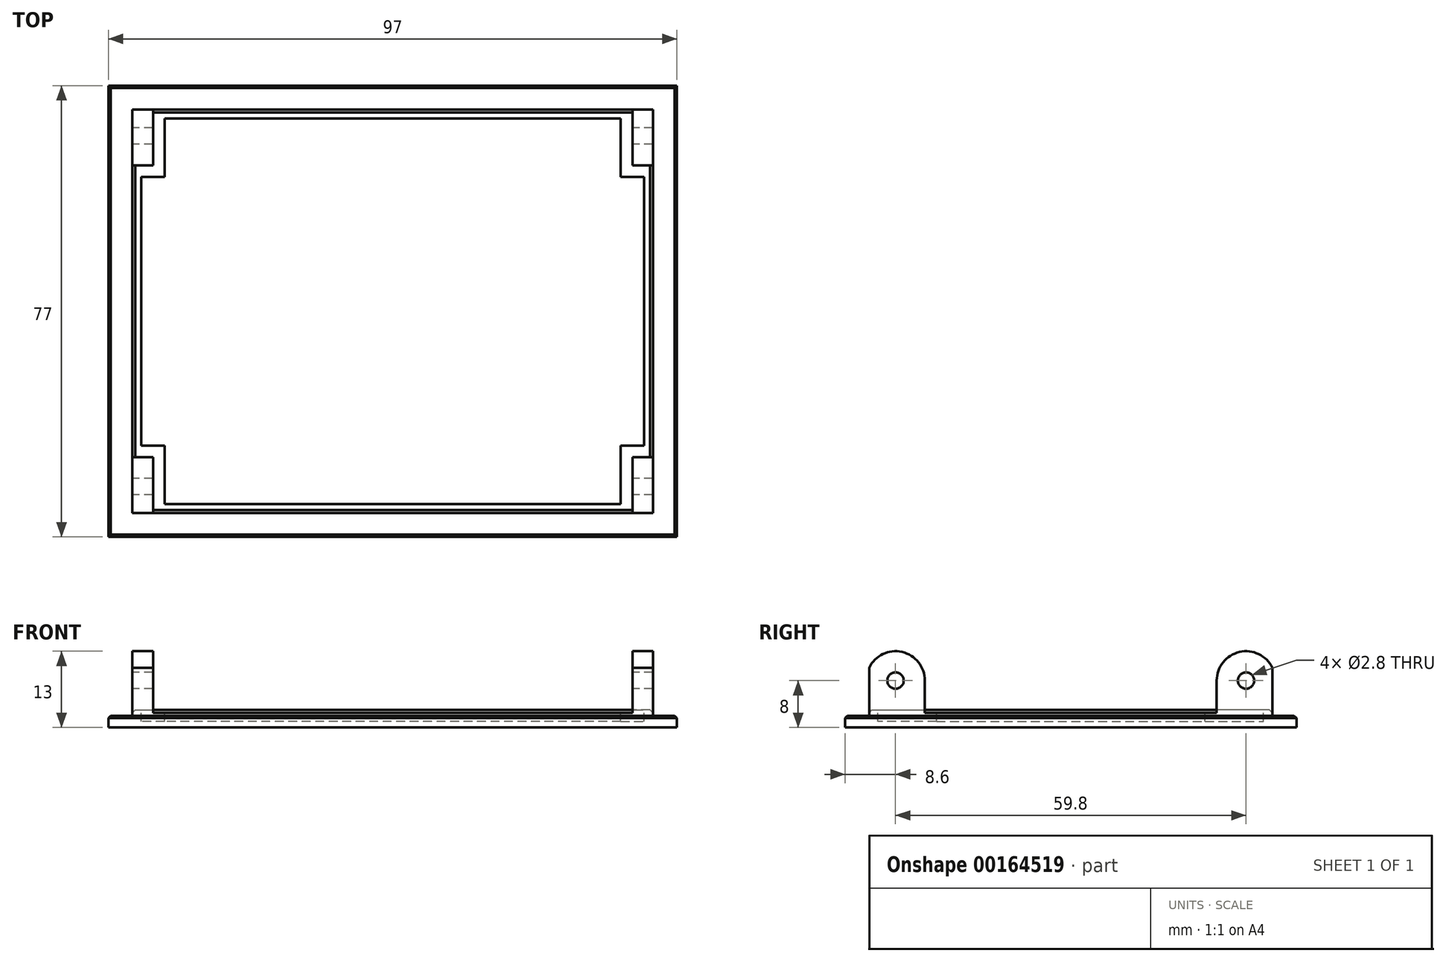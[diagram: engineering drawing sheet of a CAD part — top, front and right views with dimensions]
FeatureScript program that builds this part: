
annotation { "Feature Type Name" : "Feature", "Feature Type Description" : "" }
export const myFeature = defineFeature(function(context is Context, id is Id, definition is map)
    precondition{}
    {
        {
            var Q0;
            Q0=qCreatedBy(makeId("Top.planeOp"),FACE);
            var sketch = newSketch(context, id + "F0", { "sketchPlane" : qUnion([Q0])});
            skLineSegment(sketch, "E0.bottom", {"start": v(48.5, 38.5) * mm, "end": v(-48.5, 38.5) * mm});
            skLineSegment(sketch, "E0.top", {"start": v(48.5, -38.5) * mm, "end": v(-48.5, -38.5) * mm});
            skLineSegment(sketch, "E0.left", {"start": v(48.5, 38.5) * mm, "end": v(48.5, -38.5) * mm});
            skLineSegment(sketch, "E0.right", {"start": v(-48.5, 38.5) * mm, "end": v(-48.5, -38.5) * mm});
            skPoint(sketch, "E0.middle", {"position": v(0, 0) * mm});
            skSolve(sketch);
        }
        {
            var Q0;
            Q0 = qSketchRegion(id + "F0", true);
            extrude(context, id + "F1", {"entities" : qUnion([Q0]), "depth" : 2 * mm});
        }
        {
            var Q0;
            Q0=makeQuery(id+"F1.opExtrude","CAP_FACE",FACE,{"disambiguationData":[OSD([sQuery(id+"F0.wireOp",EDGE,"E0.bottom"),sQuery(id+"F0.wireOp",EDGE,"E0.top"),sQuery(id+"F0.wireOp",EDGE,"E0.left"),sQuery(id+"F0.wireOp",EDGE,"E0.right")])],"isStart":false});
            var sketch = newSketch(context, id + "F2", { "sketchPlane" : qUnion([Q0])});
            skLineSegment(sketch, "E1.0", {"start": v(44.9, -34.9) * mm, "end": v(44.9, 34.9) * mm});
            skLineSegment(sketch, "E1.1", {"start": v(-44.9, -34.9) * mm, "end": v(44.9, -34.9) * mm});
            skLineSegment(sketch, "E1.2", {"start": v(-44.9, 34.9) * mm, "end": v(-44.9, -34.9) * mm});
            skLineSegment(sketch, "E1.3", {"start": v(44.9, 34.9) * mm, "end": v(-44.9, 34.9) * mm});
            skSolve(sketch);
        }
        {
            var Q0;
            Q0 = qSketchRegion(id + "F2", true);
            extrude(context, id + "F3", {"entities" : qUnion([Q0]), "operationType" : NewBodyOperationType.ADD, "depth" : 1 * mm});
        }
        {
            var Q0;
            Q0=makeQuery(id+"F3.opExtrude","CAP_FACE",FACE,{"disambiguationData":[OSD([sQuery(id+"F2.wireOp",EDGE,"E1.0"),sQuery(id+"F2.wireOp",EDGE,"E1.1"),sQuery(id+"F2.wireOp",EDGE,"E1.2"),sQuery(id+"F2.wireOp",EDGE,"E1.3")])],"isStart":false});
            var sketch = newSketch(context, id + "F4", { "sketchPlane" : qUnion([Q0])});
            skLineSegment(sketch, "E2.bottom", {"start": v(-44.9, 34.9) * mm, "end": v(-40.9, 34.9) * mm});
            skLineSegment(sketch, "E2.top", {"start": v(-44.9, 24.9) * mm, "end": v(-40.9, 24.9) * mm});
            skLineSegment(sketch, "E2.left", {"start": v(-44.9, 34.9) * mm, "end": v(-44.9, 24.9) * mm});
            skLineSegment(sketch, "E2.right", {"start": v(-40.9, 34.9) * mm, "end": v(-40.9, 24.9) * mm});
            skLineSegment(sketch, "E3", {"start": v(0, 34.9) * mm, "end": v(0, -34.9) * mm, "construction": true});
            skLineSegment(sketch, "E4", {"start": v(-44.9, 0) * mm, "end": v(44.9, 0) * mm, "construction": true});
            skLineSegment(sketch, "E5.MirrorCS", {"start": v(40.9, 34.9) * mm, "end": v(40.9, 24.9) * mm});
            skLineSegment(sketch, "E6.MirrorCS", {"start": v(44.9, 34.9) * mm, "end": v(44.9, 24.9) * mm});
            skLineSegment(sketch, "E7.MirrorCS", {"start": v(44.9, 34.9) * mm, "end": v(40.9, 34.9) * mm});
            skLineSegment(sketch, "E8.MirrorCS", {"start": v(44.9, 24.9) * mm, "end": v(40.9, 24.9) * mm});
            skLineSegment(sketch, "E9.MirrorCS", {"start": v(-40.9, -34.9) * mm, "end": v(-40.9, -24.9) * mm});
            skLineSegment(sketch, "E10.MirrorCS", {"start": v(-44.9, -34.9) * mm, "end": v(-44.9, -24.9) * mm});
            skLineSegment(sketch, "E11.MirrorCS", {"start": v(-44.9, -24.9) * mm, "end": v(-40.9, -24.9) * mm});
            skLineSegment(sketch, "E12.MirrorCS", {"start": v(-44.9, -34.9) * mm, "end": v(-40.9, -34.9) * mm});
            skLineSegment(sketch, "E13.MirrorCS", {"start": v(40.9, -34.9) * mm, "end": v(40.9, -24.9) * mm});
            skLineSegment(sketch, "E14.MirrorCS", {"start": v(44.9, -34.9) * mm, "end": v(44.9, -24.9) * mm});
            skLineSegment(sketch, "E15.MirrorCS", {"start": v(44.9, -34.9) * mm, "end": v(40.9, -34.9) * mm});
            skLineSegment(sketch, "E16.MirrorCS", {"start": v(44.9, -24.9) * mm, "end": v(40.9, -24.9) * mm});
            skSolve(sketch);
        }
        {
            var Q0;
            Q0 = qSketchRegion(id + "F4", true);
            extrude(context, id + "F5", {"entities" : qUnion([Q0]), "operationType" : NewBodyOperationType.ADD, "depth" : 10 * mm});
        }
        {
            var Q0;
            Q0=makeQuery(id+"F5.opExtrude","CAP_EDGE",EDGE,{"disambiguationData":[OSD([sQuery(id+"F4.wireOp",EDGE,"E7.MirrorCS")])],"isStart":false});
            var Q1;
            Q1=makeQuery(id+"F5.opExtrude","CAP_EDGE",EDGE,{"disambiguationData":[OSD([sQuery(id+"F4.wireOp",EDGE,"E8.MirrorCS")])],"isStart":false});
            var Q2;
            Q2=makeQuery(id+"F5.opExtrude","CAP_EDGE",EDGE,{"disambiguationData":[OSD([sQuery(id+"F4.wireOp",EDGE,"E16.MirrorCS")])],"isStart":false});
            var Q3;
            Q3=makeQuery(id+"F5.opExtrude","CAP_EDGE",EDGE,{"disambiguationData":[OSD([sQuery(id+"F4.wireOp",EDGE,"E15.MirrorCS")])],"isStart":false});
            var Q4;
            Q4=makeQuery(id+"F5.opExtrude","CAP_EDGE",EDGE,{"disambiguationData":[OSD([sQuery(id+"F4.wireOp",EDGE,"E11.MirrorCS")])],"isStart":false});
            var Q5;
            Q5=makeQuery(id+"F5.opExtrude","CAP_EDGE",EDGE,{"disambiguationData":[OSD([sQuery(id+"F4.wireOp",EDGE,"E12.MirrorCS")])],"isStart":false});
            var Q6;
            Q6=makeQuery(id+"F5.opExtrude","CAP_EDGE",EDGE,{"disambiguationData":[OSD([sQuery(id+"F4.wireOp",EDGE,"E2.bottom")])],"isStart":false});
            var Q7;
            Q7=makeQuery(id+"F5.opExtrude","CAP_EDGE",EDGE,{"disambiguationData":[OSD([sQuery(id+"F4.wireOp",EDGE,"E2.top")])],"isStart":false});
            fillet(context, id + "F6", {"entities" : qUnion([Q0, Q1, Q2, Q3, Q4, Q5, Q6, Q7]), "radius" : 5 * mm, "tangentPropagation" : true, "allowEdgeOverflow" : false});
        }
        {
            var Q0;
            Q0=makeQuery(id+"F5.boolean.opBoolean","MERGE",FACE,{"derivedFrom":[makeQuery(id+"F3.opExtrude","SWEPT_FACE",FACE,{"disambiguationData":[OSD([sQuery(id+"F2.wireOp",EDGE,"E1.2")])]}),makeQuery(id+"F5.opExtrude","SWEPT_FACE",FACE,{"disambiguationData":[OSD([sQuery(id+"F4.wireOp",EDGE,"E2.left")])]}),makeQuery(id+"F5.opExtrude","SWEPT_FACE",FACE,{"disambiguationData":[OSD([sQuery(id+"F4.wireOp",EDGE,"E10.MirrorCS")])]})]});
            var sketch = newSketch(context, id + "F7", { "sketchPlane" : qUnion([Q0])});
            skCircle(sketch, "E17", {"center": v(-29.9, 8) * mm, "radius": 1.4 * mm});
            skCircle(sketch, "E18", {"center": v(29.9, 8) * mm, "radius": 1.4 * mm});
            skSolve(sketch);
        }
        {
            var Q0;
            Q0 = qSketchRegion(id + "F7", true);
            extrude(context, id + "F8", {"entities" : qUnion([Q0]), "operationType" : NewBodyOperationType.REMOVE, "endBound" : BoundingType.THROUGH_ALL, "oppositeDirection" : true, "depth" : 25 * mm});
        }
        {
            var Q0;
            Q0=makeQuery(id+"F3.opExtrude","CAP_FACE",FACE,{"disambiguationData":[OSD([sQuery(id+"F2.wireOp",EDGE,"E1.0"),sQuery(id+"F2.wireOp",EDGE,"E1.1"),sQuery(id+"F2.wireOp",EDGE,"E1.2"),sQuery(id+"F2.wireOp",EDGE,"E1.3")])],"isStart":false});
            var sketch = newSketch(context, id + "F9", { "sketchPlane" : qUnion([Q0])});
            skLineSegment(sketch, "E19.0", {"start": v(-38.9, -22.9) * mm, "end": v(-38.9, -32.9) * mm});
            skLineSegment(sketch, "E19.1", {"start": v(42.9, 22.9) * mm, "end": v(38.9, 22.9) * mm});
            skLineSegment(sketch, "E19.2", {"start": v(42.9, -22.9) * mm, "end": v(42.9, 22.9) * mm});
            skLineSegment(sketch, "E19.3", {"start": v(38.9, -22.9) * mm, "end": v(42.9, -22.9) * mm});
            skLineSegment(sketch, "E19.4", {"start": v(38.9, -32.9) * mm, "end": v(38.9, -22.9) * mm});
            skLineSegment(sketch, "E19.5", {"start": v(38.9, 22.9) * mm, "end": v(38.9, 32.9) * mm});
            skLineSegment(sketch, "E19.6", {"start": v(-38.9, -32.9) * mm, "end": v(38.9, -32.9) * mm});
            skLineSegment(sketch, "E19.7", {"start": v(38.9, 32.9) * mm, "end": v(-38.9, 32.9) * mm});
            skLineSegment(sketch, "E19.8", {"start": v(-38.9, 32.9) * mm, "end": v(-38.9, 22.9) * mm});
            skLineSegment(sketch, "E19.9", {"start": v(-38.9, 22.9) * mm, "end": v(-42.9, 22.9) * mm});
            skLineSegment(sketch, "E19.10", {"start": v(-42.9, 22.9) * mm, "end": v(-42.9, -22.9) * mm});
            skLineSegment(sketch, "E19.11", {"start": v(-42.9, -22.9) * mm, "end": v(-38.9, -22.9) * mm});
            skSolve(sketch);
        }
        {
            var Q0;
            Q0 = qSketchRegion(id + "F9", true);
            extrude(context, id + "F10", {"entities" : qUnion([Q0]), "operationType" : NewBodyOperationType.REMOVE, "oppositeDirection" : true, "depth" : 2 * mm});
        }
        {
            var Q0;
            Q0=makeQuery(id+"F1.opExtrude","CAP_FACE",FACE,{"disambiguationData":[OSD([sQuery(id+"F0.wireOp",EDGE,"E0.bottom"),sQuery(id+"F0.wireOp",EDGE,"E0.top"),sQuery(id+"F0.wireOp",EDGE,"E0.left"),sQuery(id+"F0.wireOp",EDGE,"E0.right")])],"isStart":false});
            var sketch = newSketch(context, id + "F11", { "sketchPlane" : qUnion([Q0])});
            skLineSegment(sketch, "E20.0", {"start": v(-44.4, -34.4) * mm, "end": v(44.4, -34.4) * mm});
            skLineSegment(sketch, "E20.1", {"start": v(-44.4, 34.4) * mm, "end": v(-44.4, -34.4) * mm});
            skLineSegment(sketch, "E20.2", {"start": v(44.4, 34.4) * mm, "end": v(-44.4, 34.4) * mm});
            skLineSegment(sketch, "E20.3", {"start": v(44.4, -34.4) * mm, "end": v(44.4, 34.4) * mm});
            skLineSegment(sketch, "E21.0", {"start": v(48.5, -38.5) * mm, "end": v(-48.5, -38.5) * mm});
            skLineSegment(sketch, "E21.1", {"start": v(48.5, 38.5) * mm, "end": v(48.5, -38.5) * mm});
            skLineSegment(sketch, "E21.2", {"start": v(48.5, 38.5) * mm, "end": v(-48.5, 38.5) * mm});
            skLineSegment(sketch, "E21.3", {"start": v(-48.5, 38.5) * mm, "end": v(-48.5, -38.5) * mm});
            skSolve(sketch);
        }
        {
            var Q0;
            Q0 = qSketchRegion(id + "F11", true);
            extrude(context, id + "F12", {"entities" : qUnion([Q0]), "operationType" : NewBodyOperationType.REMOVE, "endBound" : BoundingType.THROUGH_ALL, "depth" : 25 * mm});
        }
        {
            var Q0;
            Q0=makeQuery(id+"F12.boolean.opBoolean","INTERSECT",EDGE,{"derivedFrom":[makeQuery(id+"F3.opExtrude","CAP_FACE",FACE,{"disambiguationData":[OSD([sQuery(id+"F2.wireOp",EDGE,"E1.0"),sQuery(id+"F2.wireOp",EDGE,"E1.1"),sQuery(id+"F2.wireOp",EDGE,"E1.2"),sQuery(id+"F2.wireOp",EDGE,"E1.3")])],"isStart":false}),makeQuery(id+"F12.opExtrude","SWEPT_FACE",FACE,{"disambiguationData":[OSD([sQuery(id+"F11.wireOp",EDGE,"E20.3")])]})]});
            var Q1;
            Q1=makeQuery(id+"F12.boolean.opBoolean","INTERSECT",EDGE,{"derivedFrom":[makeQuery(id+"F3.opExtrude","CAP_FACE",FACE,{"disambiguationData":[OSD([sQuery(id+"F2.wireOp",EDGE,"E1.0"),sQuery(id+"F2.wireOp",EDGE,"E1.1"),sQuery(id+"F2.wireOp",EDGE,"E1.2"),sQuery(id+"F2.wireOp",EDGE,"E1.3")])],"isStart":false}),makeQuery(id+"F12.opExtrude","SWEPT_FACE",FACE,{"disambiguationData":[OSD([sQuery(id+"F11.wireOp",EDGE,"E20.0")])]})]});
            var Q2;
            Q2=makeQuery(id+"F12.boolean.opBoolean","INTERSECT",EDGE,{"derivedFrom":[makeQuery(id+"F3.opExtrude","CAP_FACE",FACE,{"disambiguationData":[OSD([sQuery(id+"F2.wireOp",EDGE,"E1.0"),sQuery(id+"F2.wireOp",EDGE,"E1.1"),sQuery(id+"F2.wireOp",EDGE,"E1.2"),sQuery(id+"F2.wireOp",EDGE,"E1.3")])],"isStart":false}),makeQuery(id+"F12.opExtrude","SWEPT_FACE",FACE,{"disambiguationData":[OSD([sQuery(id+"F11.wireOp",EDGE,"E20.1")])]})]});
            var Q3;
            Q3=makeQuery(id+"F12.boolean.opBoolean","INTERSECT",EDGE,{"derivedFrom":[makeQuery(id+"F3.opExtrude","CAP_FACE",FACE,{"disambiguationData":[OSD([sQuery(id+"F2.wireOp",EDGE,"E1.0"),sQuery(id+"F2.wireOp",EDGE,"E1.1"),sQuery(id+"F2.wireOp",EDGE,"E1.2"),sQuery(id+"F2.wireOp",EDGE,"E1.3")])],"isStart":false}),makeQuery(id+"F12.opExtrude","SWEPT_FACE",FACE,{"disambiguationData":[OSD([sQuery(id+"F11.wireOp",EDGE,"E20.2")])]})]});
            chamfer(context, id + "F13", {"entities" : qUnion([Q0, Q1, Q2, Q3]), "width" : 0.5 * mm, "tangentPropagation" : true});
        }
        {
            var Q0;
            Q0=makeQuery(id+"F1.opExtrude","CAP_EDGE",EDGE,{"disambiguationData":[OSD([sQuery(id+"F0.wireOp",EDGE,"E0.right")])],"isStart":false});
            var Q1;
            Q1=makeQuery(id+"F1.opExtrude","CAP_EDGE",EDGE,{"disambiguationData":[OSD([sQuery(id+"F0.wireOp",EDGE,"E0.bottom")])],"isStart":false});
            var Q2;
            Q2=makeQuery(id+"F1.opExtrude","CAP_EDGE",EDGE,{"disambiguationData":[OSD([sQuery(id+"F0.wireOp",EDGE,"E0.left")])],"isStart":false});
            var Q3;
            Q3=makeQuery(id+"F1.opExtrude","CAP_EDGE",EDGE,{"disambiguationData":[OSD([sQuery(id+"F0.wireOp",EDGE,"E0.top")])],"isStart":false});
            chamfer(context, id + "F14", {"entities" : qUnion([Q0, Q1, Q2, Q3]), "width" : 0.4 * mm, "tangentPropagation" : true});
        }
    });
